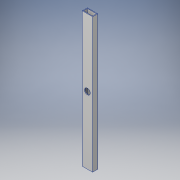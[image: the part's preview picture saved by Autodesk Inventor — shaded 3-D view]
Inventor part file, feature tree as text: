
AUTODESK INVENTOR PART (.ipt)
format: ipt  version: 2018 (Build 220112000, 112)  size: 112,640 bytes
history: native  units: in
note: dims shown in document units (in); Inventor stores cm internally (conversion verified against a paired STEP export)
features: extrude x2, sketch x2
ambient origin geometry x8: Origin, YZ Plane, XZ Plane, XY Plane, X Axis, Y Axis, Z Axis, Center Point
bodies: Solid1 (feature_tree)
feature tree (4):
  extrude  "Extrusion1"  Depth=1.0in
  extrude  "Extrusion2"  Depth=0.125in
  sketch  "Sketch1"  dims[d0=2.0in d1=1.0in]
  sketch  "Sketch2"  dims[d2=0.125in d3=0.125in d4=0.125in d5=0.125in d6=26.0in d7=0.0in d8=1.125in d9=1.0in d10=0.0in]
